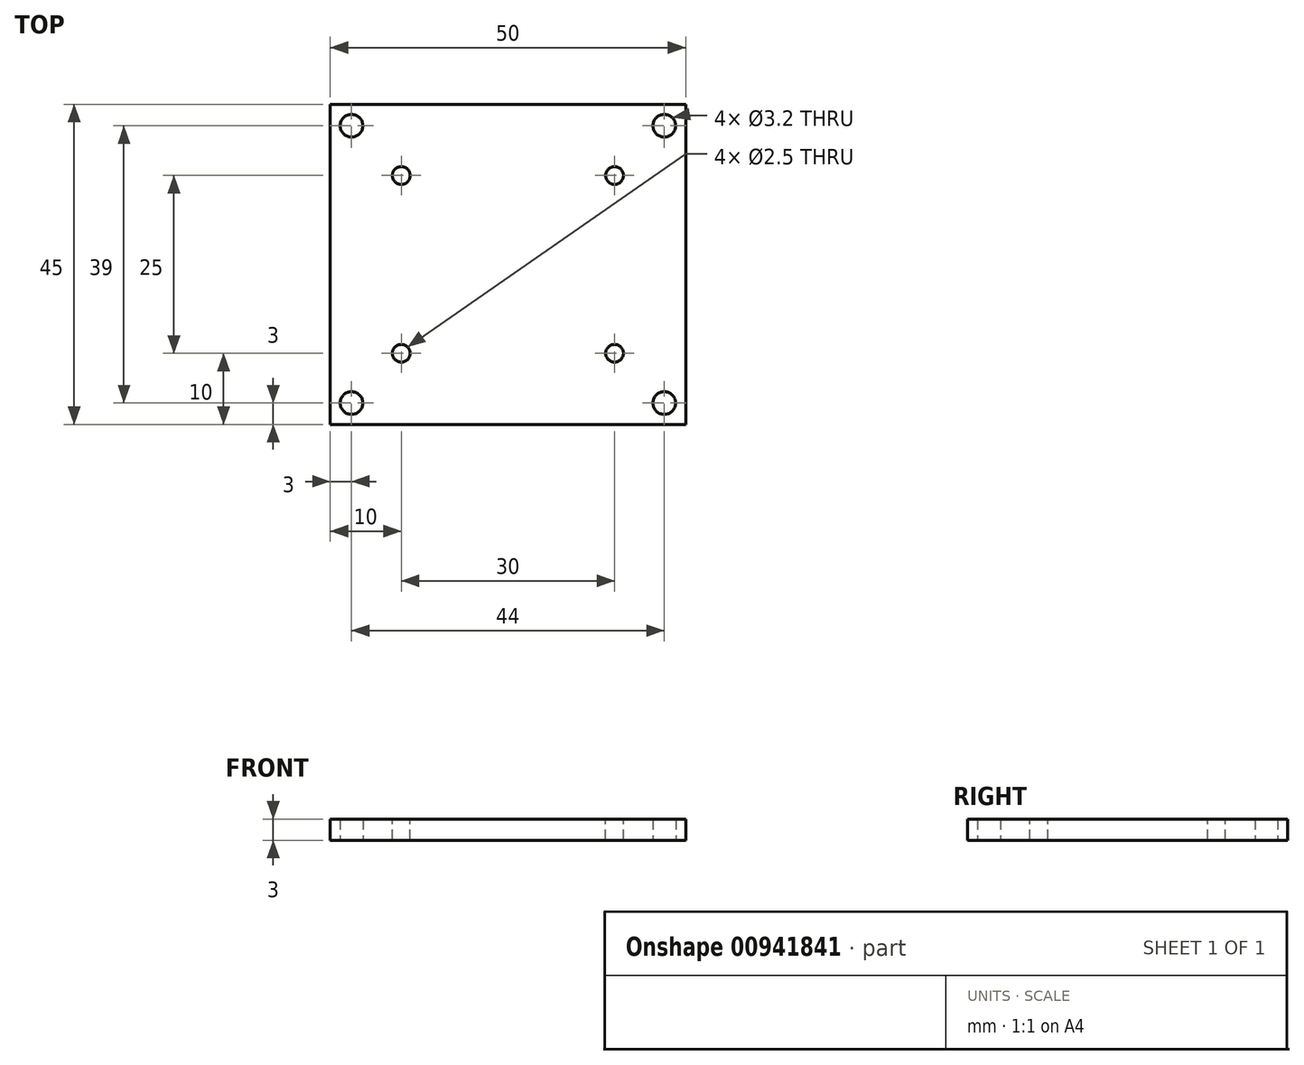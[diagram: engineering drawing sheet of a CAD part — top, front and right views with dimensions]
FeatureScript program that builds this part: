
annotation { "Feature Type Name" : "Feature", "Feature Type Description" : "" }
export const myFeature = defineFeature(function(context is Context, id is Id, definition is map)
    precondition{}
    {
        {
            var Q0;
            Q0=qCreatedBy(makeId("Top.planeOp"),FACE);
            var sketch = newSketch(context, id + "F0", { "sketchPlane" : qUnion([Q0])});
            skLineSegment(sketch, "E0.bottom", {"start": v(25, -22.5) * mm, "end": v(-25, -22.5) * mm});
            skLineSegment(sketch, "E0.top", {"start": v(25, 22.5) * mm, "end": v(-25, 22.5) * mm});
            skLineSegment(sketch, "E0.left", {"start": v(25, -22.5) * mm, "end": v(25, 22.5) * mm});
            skLineSegment(sketch, "E0.right", {"start": v(-25, -22.5) * mm, "end": v(-25, 22.5) * mm});
            skPoint(sketch, "E0.middle", {"position": v(0, 0) * mm});
            skLineSegment(sketch, "E1.bottom", {"start": v(17.5, -15) * mm, "end": v(-17.5, -15) * mm, "construction": true});
            skLineSegment(sketch, "E1.top", {"start": v(17.5, 15) * mm, "end": v(-17.5, 15) * mm, "construction": true});
            skLineSegment(sketch, "E1.left", {"start": v(17.5, -15) * mm, "end": v(17.5, 15) * mm, "construction": true});
            skLineSegment(sketch, "E1.right", {"start": v(-17.5, -15) * mm, "end": v(-17.5, 15) * mm, "construction": true});
            skCircle(sketch, "E2", {"center": v(-22, 19.5) * mm, "radius": 1.6 * mm});
            skCircle(sketch, "E3.0.1.0", {"center": v(-22, -19.5) * mm, "radius": 1.6 * mm});
            skCircle(sketch, "E3.1.0.0", {"center": v(22, 19.5) * mm, "radius": 1.6 * mm});
            skCircle(sketch, "E3.1.1.0", {"center": v(22, -19.5) * mm, "radius": 1.6 * mm});
            skLineSegment(sketch, "E3.direction2", {"start": v(-22, 19.5) * mm, "end": v(-22, -19.5) * mm, "construction": true});
            skLineSegment(sketch, "E4", {"start": v(-22, 19.5) * mm, "end": v(22, 19.5) * mm, "construction": true});
            skSolve(sketch);
        }
        {
            var Q0;
            Q0 = qSketchRegion(id + "F0", true);
            extrude(context, id + "F1", {"entities" : qUnion([Q0]), "depth" : 3 * mm, "offsetDistance" : 25 * mm});
        }
        {
            var Q0;
            Q0=makeQuery(id+"F1.opExtrude","CAP_FACE",FACE,{"disambiguationData":[OSD([sQuery(id+"F0.wireOp",EDGE,"E0.bottom"),sQuery(id+"F0.wireOp",EDGE,"E0.top"),sQuery(id+"F0.wireOp",EDGE,"E0.left"),sQuery(id+"F0.wireOp",EDGE,"E0.right"),sQuery(id+"F0.wireOp",EDGE,"E2"),sQuery(id+"F0.wireOp",EDGE,"E3.0.1.0"),sQuery(id+"F0.wireOp",EDGE,"E3.1.0.0"),sQuery(id+"F0.wireOp",EDGE,"E3.1.1.0")])],"isStart":false});
            var sketch = newSketch(context, id + "F2", { "sketchPlane" : qUnion([Q0])});
            skLineSegment(sketch, "E5.bottom", {"start": v(15, -12.5) * mm, "end": v(-15, -12.5) * mm, "construction": true});
            skLineSegment(sketch, "E5.top", {"start": v(15, 12.5) * mm, "end": v(-15, 12.5) * mm, "construction": true});
            skLineSegment(sketch, "E5.left", {"start": v(15, -12.5) * mm, "end": v(15, 12.5) * mm, "construction": true});
            skLineSegment(sketch, "E5.right", {"start": v(-15, -12.5) * mm, "end": v(-15, 12.5) * mm, "construction": true});
            skPoint(sketch, "E5.middle", {"position": v(0, 0) * mm});
            skSolve(sketch);
        }
        {
            var Q0;
            Q0=sQuery(id+"F2.wireOp",VERTEX,"E5.top.end");
            var Q1;
            Q1=sQuery(id+"F2.wireOp",VERTEX,"E5.top.start");
            var Q2;
            Q2=sQuery(id+"F2.wireOp",VERTEX,"E5.bottom.start");
            var Q3;
            Q3=sQuery(id+"F2.wireOp",VERTEX,"E5.bottom.end");
            var Q4;
            Q4=makeQuery(id+"F1.opExtrude","SWEPT_BODY",BODY,{"disambiguationData":[OSD([sQuery(id+"F0.wireOp",EDGE,"E0.bottom"),sQuery(id+"F0.wireOp",EDGE,"E0.top"),sQuery(id+"F0.wireOp",EDGE,"E0.left"),sQuery(id+"F0.wireOp",EDGE,"E0.right"),sQuery(id+"F0.wireOp",EDGE,"E2"),sQuery(id+"F0.wireOp",EDGE,"E3.0.1.0"),sQuery(id+"F0.wireOp",EDGE,"E3.1.0.0"),sQuery(id+"F0.wireOp",EDGE,"E3.1.1.0")])]});
            hole(context, id + "F3", {"style" : HoleStyle.SIMPLE, "endStyle" : HoleEndStyle.THROUGH, "standardTappedOrClearance" : lookupTablePath({ "standard" : "ISO", "engagement" : "75%", "pitch" : "0.5 mm", "size" : "M3", "type" : "Tapped" }), "standardBlindInLast" : lookupTablePath({ "standard" : "ISO", "fit" : "Normal", "engagement" : "75%", "pitch" : "0.5 mm", "size" : "M3", "type" : "Clearance & tapped" }), "holeDiameter" : 2.5 * mm, "majorDiameter" : 3 * mm, "showTappedDepth" : true, "isTappedThrough" : true, "tappedDepth" : 12 * mm, "tapClearance" : 3, "locations" : qUnion([Q0, Q1, Q2, Q3]), "scope" : qUnion([Q4])});
        }
    });
